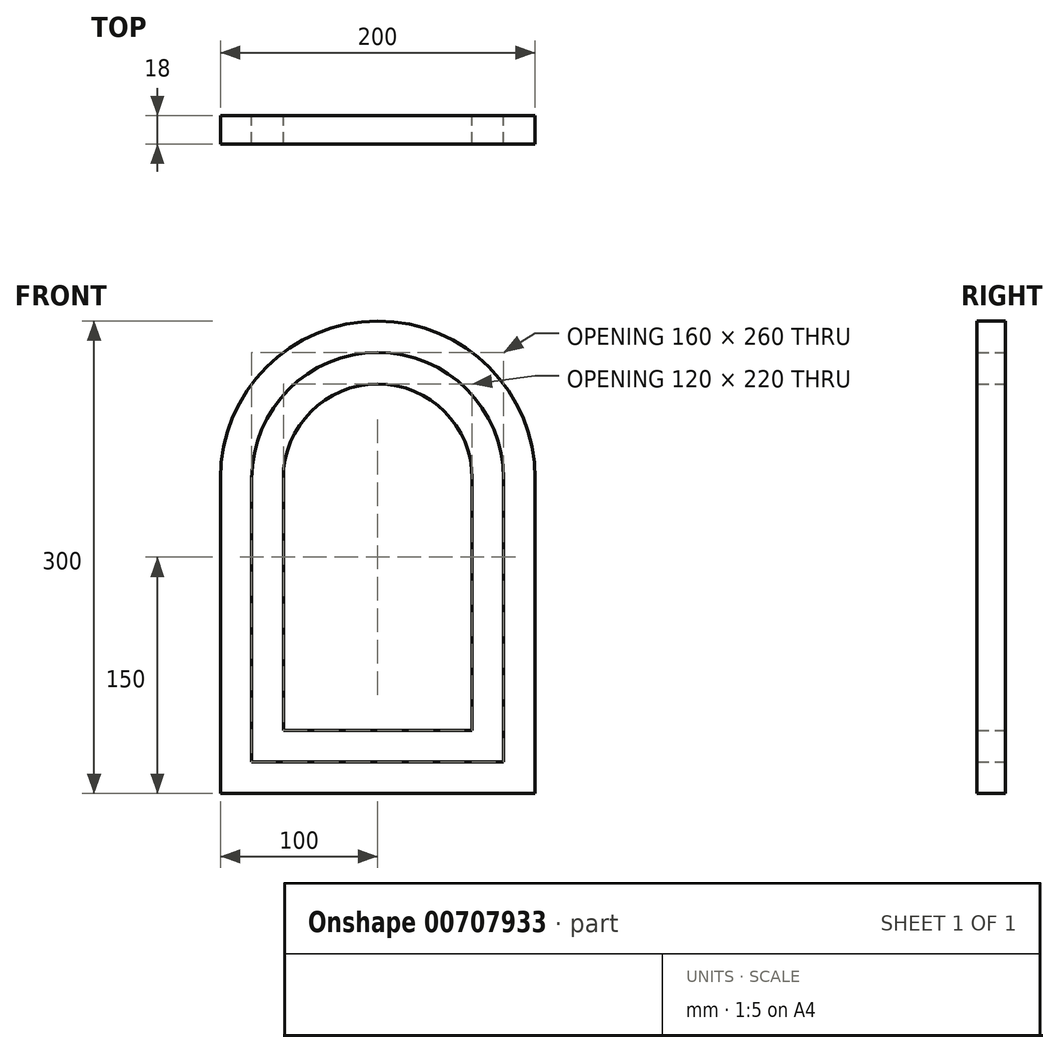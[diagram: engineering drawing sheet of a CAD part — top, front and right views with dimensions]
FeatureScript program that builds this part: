
annotation { "Feature Type Name" : "Feature", "Feature Type Description" : "" }
export const myFeature = defineFeature(function(context is Context, id is Id, definition is map)
    precondition{}
    {
        {
            var Q0;
            Q0=qCreatedBy(makeId("Front.planeOp"),FACE);
            var sketch = newSketch(context, id + "F0", { "sketchPlane" : qUnion([Q0])});
            skLineSegment(sketch, "E0.bottom", {"start": v(0, 0) * mm, "end": v(200, 0) * mm});
            skLineSegment(sketch, "E0.right", {"start": v(200, 0) * mm, "end": v(200, 200) * mm});
            skArc(sketch, "E1", {"start": v(200, 200) * mm, "mid": v(100, 300) * mm, "end": v(0, 200) * mm});
            skLineSegment(sketch, "E2", {"start": v(0, 200) * mm, "end": v(0, 0) * mm});
            skLineSegment(sketch, "E3.0", {"start": v(20, 20) * mm, "end": v(180, 20) * mm});
            skLineSegment(sketch, "E3.1", {"start": v(20, 200) * mm, "end": v(20, 20) * mm});
            skArc(sketch, "E3.2", {"start": v(180, 200) * mm, "mid": v(100, 280) * mm, "end": v(20, 200) * mm});
            skLineSegment(sketch, "E3.3", {"start": v(180, 20) * mm, "end": v(180, 200) * mm});
            skArc(sketch, "E4.0", {"start": v(160, 200) * mm, "mid": v(100, 260) * mm, "end": v(40, 200) * mm});
            skLineSegment(sketch, "E4.1", {"start": v(160, 40) * mm, "end": v(160, 200) * mm});
            skLineSegment(sketch, "E4.2", {"start": v(40, 40) * mm, "end": v(160, 40) * mm});
            skLineSegment(sketch, "E4.3", {"start": v(40, 200) * mm, "end": v(40, 40) * mm});
            skSolve(sketch);
        }
        {
            var Q0;
            Q0=makeQuery(id+"F0.imprint","IMPRINT",FACE,{"disambiguationData":[TD([[makeQuery(id+"F0.imprint","IMPRINT",EDGE,{"derivedFrom":sQuery(id+"F0.wireOp",EDGE,"E3.0")}),1.0]])]});
            extrude(context, id + "F1", {"entities" : qUnion([Q0]), "depth" : 18 * mm, "offsetDistance" : 25 * mm});
        }
        {
            var Q0;
            Q0=makeQuery(id+"F0.imprint","IMPRINT",FACE,{"disambiguationData":[TD([[makeQuery(id+"F0.imprint","IMPRINT",EDGE,{"derivedFrom":sQuery(id+"F0.wireOp",EDGE,"E0.bottom")}),1.0]])]});
            extrude(context, id + "F2", {"entities" : qUnion([Q0]), "depth" : 18 * mm, "offsetDistance" : 25 * mm});
        }
    });
